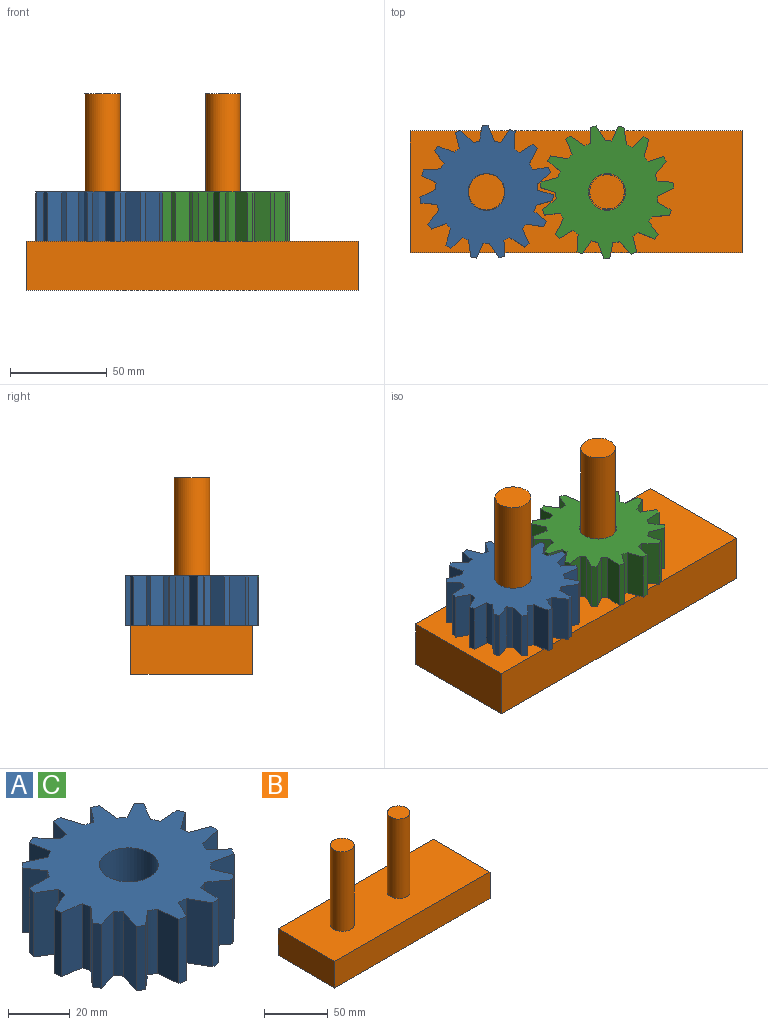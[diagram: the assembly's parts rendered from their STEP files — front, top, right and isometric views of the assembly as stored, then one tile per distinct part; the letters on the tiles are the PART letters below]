
ASSEMBLY  parts=3 mates=2
PART A: 63 faces, bbox 68.8x68.7x25.4 mm
  f0: plane 25.4x3mm, normal (0,1,0), area 76.2mm2, adj f1,f59,f60,f61
  f1: plane 25.4x8.05mm, normal (-0.97,0.23,0), area 210.2mm2, adj f0,f2,f60,f61
  f2: cylinder r=26.45mm len=25.4mm, axis (0,0,-1), area 84.4mm2, adj f1,f3,f60,f61
  f3: plane 25.4x6.74mm, normal (0.75,0.67,0), area 229.8mm2, adj f2,f4,f60,f61
  f4: plane 25.4x2.74mm, normal (-0.41,0.91,0), area 76.2mm2, adj f3,f5,f60,f61
  f5: plane 25.4x8.14mm, normal (-0.98,-0.18,0), area 210.2mm2, adj f4,f6,f60,f61
  f6: cylinder r=26.45mm len=25.4mm, axis (0,0,-1), area 84.4mm2, adj f5,f7,f60,f61
  f7: plane 25.4x8.25mm, normal (0.41,0.91,0), area 229.8mm2, adj f6,f8,f60,f61
  f8: plane 25.4x2.23mm, normal (-0.74,0.67,0), area 76.2mm2, adj f7,f9,f60,f61
  f9: plane 25.4x6.82mm, normal (-0.82,-0.57,0), area 210.2mm2, adj f8,f10,f60,f61
  f10: cylinder r=26.45mm len=25.4mm, axis (0,0,-1), area 84.4mm2, adj f9,f11,f60,f61
  f11: plane 25.4x9.05mm, normal (0,1,0), area 229.8mm2, adj f10,f12,f60,f61
  f12: plane 25.4x2.85mm, normal (-0.95,0.31,0), area 76.2mm2, adj f11,f13,f60,f61
  f13: plane 25.4x7.05mm, normal (-0.52,-0.85,0), area 210.2mm2, adj f12,f14,f60,f61
  f14: cylinder r=26.45mm len=25.4mm, axis (0,0,-1), area 84.4mm2, adj f13,f15,f60,f61
  f15: plane 25.4x8.28mm, normal (-0.4,0.91,0), area 229.8mm2, adj f14,f16,f60,f61
  f16: plane 25.4x2.99mm, normal (-0.99,-0.1,0), area 76.2mm2, adj f15,f17,f60,f61
  f17: plane 25.4x8.2mm, normal (-0.13,-0.99,0), area 210.2mm2, adj f16,f18,f60,f61
  f18: cylinder r=26.45mm len=25.4mm, axis (0,0,-1), area 84.4mm2, adj f17,f19,f60,f61
  f19: plane 25.4x6.71mm, normal (-0.74,0.67,0), area 229.8mm2, adj f18,f20,f60,f61
  f20: plane 25.4x2.6mm, normal (-0.87,-0.5,0), area 76.2mm2, adj f19,f21,f60,f61
  f21: plane 25.4x7.94mm, normal (0.28,-0.96,0), area 210.2mm2, adj f20,f22,f60,f61
  f22: cylinder r=26.45mm len=25.4mm, axis (0,0,-1), area 84.4mm2, adj f21,f23,f60,f61
  f23: plane 25.4x8.6mm, normal (-0.95,0.31,0), area 229.8mm2, adj f22,f24,f60,f61
  f24: plane 25.4x2.43mm, normal (-0.59,-0.81,0), area 76.2mm2, adj f23,f25,f60,f61
  f25: plane 25.4x6.3mm, normal (0.65,-0.76,0), area 210.2mm2, adj f24,f26,f60,f61
  f26: cylinder r=26.45mm len=25.4mm, axis (0,0,-1), area 84.4mm2, adj f25,f27,f60,f61
  f27: plane 25.4x9mm, normal (-0.99,-0.1,0), area 229.8mm2, adj f26,f28,f60,f61
  f28: plane 25.4x2.94mm, normal (-0.21,-0.98,0), area 76.2mm2, adj f27,f29,f60,f61
  f29: plane 25.4x7.47mm, normal (0.9,-0.43,0), area 210.2mm2, adj f28,f30,f60,f61
  f30: cylinder r=26.45mm len=25.4mm, axis (0,0,-1), area 84.4mm2, adj f29,f31,f60,f61
  f31: plane 25.4x7.85mm, normal (-0.87,-0.5,0), area 229.8mm2, adj f30,f32,f60,f61
  f32: plane 25.4x2.94mm, normal (0.21,-0.98,0), area 76.2mm2, adj f31,f33,f60,f61
  f33: plane 25.4x8.27mm, normal (1,-0.03,0), area 210.2mm2, adj f32,f34,f60,f61
  f34: cylinder r=26.45mm len=25.4mm, axis (0,0,-1), area 84.4mm2, adj f33,f35,f60,f61
  f35: plane 25.4x7.3mm, normal (-0.59,-0.81,0), area 229.8mm2, adj f34,f36,f60,f61
  f36: plane 25.4x2.43mm, normal (0.59,-0.81,0), area 76.2mm2, adj f35,f37,f60,f61
  f37: plane 25.4x7.65mm, normal (0.92,0.38,0), area 210.2mm2, adj f36,f38,f60,f61
  f38: cylinder r=26.45mm len=25.4mm, axis (0,0,-1), area 84.4mm2, adj f37,f39,f60,f61
  f39: plane 25.4x8.84mm, normal (-0.21,-0.98,0), area 229.8mm2, adj f38,f40,f60,f61
  f40: plane 25.4x2.6mm, normal (0.87,-0.5,0), area 76.2mm2, adj f39,f41,f60,f61
  f41: plane 25.4x6mm, normal (0.69,0.72,0), area 210.2mm2, adj f40,f42,f60,f61
  f42: cylinder r=26.45mm len=25.4mm, axis (0,0,-1), area 84.4mm2, adj f41,f43,f60,f61
  f43: plane 25.4x8.85mm, normal (0.21,-0.98,0), area 229.8mm2, adj f42,f44,f60,f61
  f44: plane 25.4x2.99mm, normal (0.99,-0.1,0), area 76.2mm2, adj f43,f45,f60,f61
  f45: plane 25.4x7.8mm, normal (0.33,0.94,0), area 210.2mm2, adj f44,f46,f60,f61
  f46: cylinder r=26.45mm len=25.4mm, axis (0,0,-1), area 84.4mm2, adj f45,f47,f60,f61
  f47: plane 25.4x7.33mm, normal (0.59,-0.81,0), area 229.8mm2, adj f46,f48,f60,f61
  f48: plane 25.4x2.85mm, normal (0.95,0.31,0), area 76.2mm2, adj f47,f49,f60,f61
  f49: plane 25.4x8.25mm, normal (-0.08,1,0), area 210.2mm2, adj f48,f50,f60,f61
  f50: cylinder r=26.45mm len=25.4mm, axis (0,0,-1), area 84.4mm2, adj f49,f51,f60,f61
  f51: plane 25.4x7.82mm, normal (0.86,-0.5,0), area 229.8mm2, adj f50,f52,f60,f61
  f52: plane 25.4x2.23mm, normal (0.74,0.67,0), area 76.2mm2, adj f51,f53,f60,f61
  f53: plane 25.4x7.28mm, normal (-0.48,0.88,0), area 210.2mm2, adj f52,f54,f60,f61
  f54: cylinder r=26.45mm len=25.4mm, axis (0,0,-1), area 84.4mm2, adj f53,f55,f60,f61
  f55: plane 25.4x8.99mm, normal (0.99,-0.11,0), area 229.8mm2, adj f54,f56,f60,f61
  f56: plane 25.4x2.74mm, normal (0.41,0.91,0), area 76.2mm2, adj f55,f57,f60,f61
  f57: plane 25.4x6.56mm, normal (-0.79,0.61,0), area 210.2mm2, adj f56,f58,f60,f61
  f58: cylinder r=26.45mm len=25.4mm, axis (0,0,-1), area 84.4mm2, adj f57,f59,f60,f61
  f59: plane 25.4x8.61mm, normal (0.95,0.31,0), area 229.8mm2, adj f0,f58,f60,f61
  f60: plane 68.79x68.73mm, normal (0,0,1), area 2558.8mm2, adj f0,f1,f2,f3,f4,f5,f6,f7
  f61: plane 68.79x68.73mm, normal (0,0,-1), area 2558.8mm2, adj f0,f1,f2,f3,f4,f5,f6,f7
  f62: cylinder r=9.53mm len=25.4mm, axis (0,0,1), area 1520.1mm2, adj f60,f61
PART B: 10 faces, bbox 171.5x62.9x101.6 mm
  f0: plane 171.49x25.4mm, normal (0,1,0), area 4355.7mm2, adj f1,f3,f4,f5
  f1: plane 62.93x25.4mm, normal (-1,0,0), area 1598.5mm2, adj f0,f2,f4,f5
  f2: plane 171.49x25.4mm, normal (0,-1,0), area 4355.7mm2, adj f1,f3,f4,f5
  f3: plane 62.93x25.4mm, normal (1,0,0), area 1598.5mm2, adj f0,f2,f4,f5
  f4: plane 171.49x62.93mm, normal (0,0,1), area 10274mm2, adj f0,f1,f2,f3,f6,f8
  f5: plane 171.49x62.93mm, normal (0,0,-1), area 10792.3mm2, adj f0,f1,f2,f3
  f6: cylinder r=9.27mm len=76.2mm, axis (0,0,-1), area 4438.8mm2, adj f4,f7
  f7: plane 18.54x18.54mm, normal (0,0,1), area 270mm2, adj f6
  f8: cylinder r=8.89mm len=76.2mm, axis (0,0,-1), area 4256.3mm2, adj f4,f9
  f9: plane 17.78x17.78mm, normal (0,0,1), area 248.3mm2, adj f8
PART C: same geometry as A
PLACE A rot(axis=(0,0,1),75.7deg) t=(-46.22,-0.12,25.4)mm
PLACE B t=(-0.98,-0.12,0)mm
PLACE C rot(axis=(0,0,1),14.3deg) t=(16.01,-0.12,25.4)mm
MATE revolute C.f62 <-> B.f8  axis (0,0,-1) through (16.01,-0.12,25.4)mm
MATE revolute A.f62 <-> B.f6  axis (0,0,-1) through (-46.22,-0.12,25.4)mm
